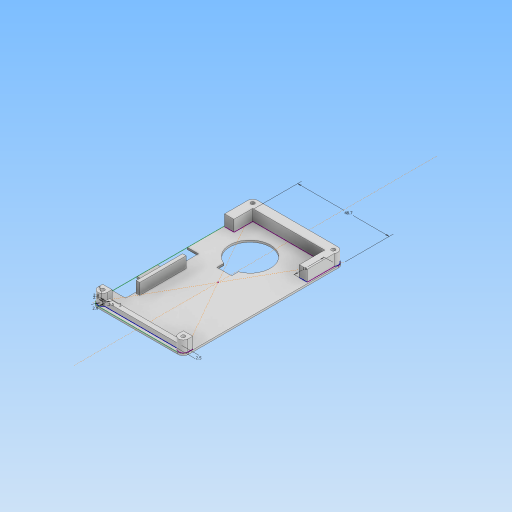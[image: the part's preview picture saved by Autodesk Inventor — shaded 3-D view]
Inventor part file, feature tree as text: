
AUTODESK INVENTOR PART (.ipt)
format: ipt  version: 2023 (Build 270158000, 158)  size: 227,840 bytes
history: native  units: mm
features: extrude x10, sketch x8
ambient origin geometry x8: Origin, YZ Plane, XZ Plane, XY Plane, X Axis, Y Axis, Z Axis, Center Point
bodies: Body1 (feature_tree)
feature tree (18):
  sketch  "Sketch1"  dims[d2=3.0mm]
  sketch  "Sketch2"  dims[d16=48.7mm d17=2.0mm d18=5.0mm d19=2.5mm d20=2.5mm d21=16.0mm]
  sketch  "Sketch4"  dims[d22=6.0mm d23=2.9mm]
  sketch  "Sketch5"  dims[d24=2.9mm d25=2.9mm]
  extrude  "Extrusion2"  Depth=16.0mm
  extrude  "Extrusion3"  Depth=6.0mm
  extrude  "Extrusion4"  Depth=2.9mm
  extrude  "Extrusion5"  Depth=2.5mm TaperAngle=0.0deg
  extrude  "Extrusion6"  Depth=5.0mm TaperAngle=0.0deg
  extrude  "Extrusion7"  TaperAngle=0.0deg  [1 undecoded]
  extrude  "Extrusion8"  TaperAngle=0.0deg  [1 undecoded]
  extrude  "Extrusion9"  Depth=7.0mm
  sketch  "Sketch7"  dims[d30=5.9mm d31=0.0mm d32=5.0mm d33=0.0mm]
  extrude  "Extrusion10"  Depth=24.0mm
  extrude  "Extrusion11"  Depth=11.0mm
  sketch  "Sketch6"  dims[d26=1.0mm d27=0.0mm d28=2.5mm d29=0.0mm]
  sketch  "Sketch8"  dims[d34=0.0mm d35=0.0mm d36=0.0mm d37=0.0mm]
  sketch  "Sketch9"  dims[d38=0.0mm d39=0.0mm d41=0.0mm d42=0.0mm d43=7.0mm d45=24.0mm d46=11.0mm d47=0.0mm d48=0.0mm d49=10.0mm d50=0.0mm d52=16.0mm]
note: 2 required parameter values undecoded (feature->parameter linkage not recoverable at this tier; creation-order binding heuristic only, values carry confidence <= 0.55)
